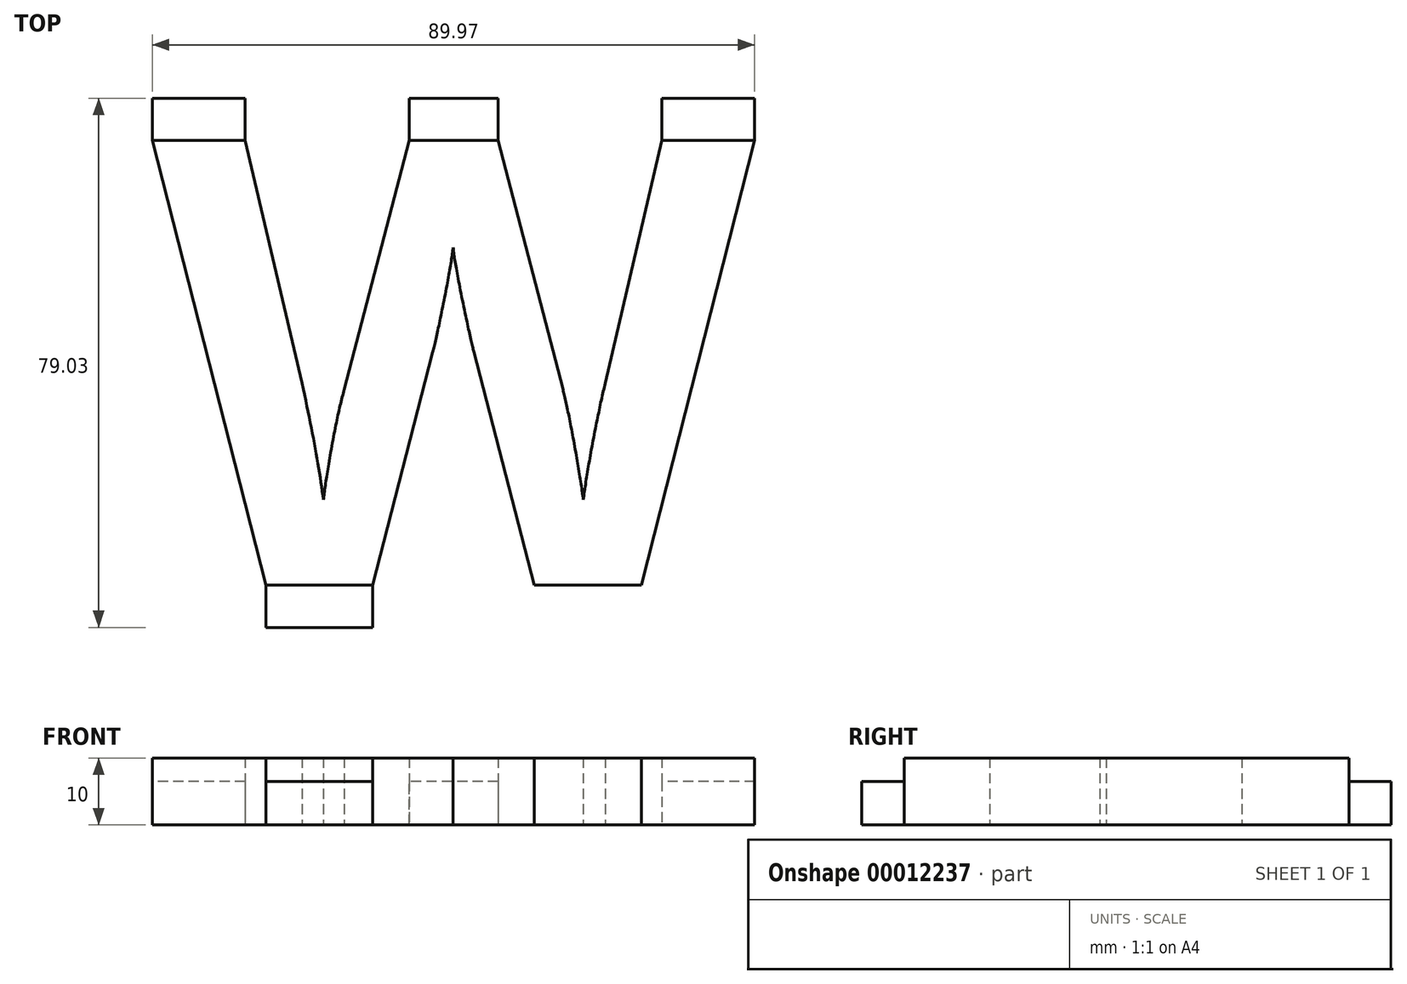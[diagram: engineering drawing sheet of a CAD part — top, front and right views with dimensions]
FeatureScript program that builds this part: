
annotation { "Feature Type Name" : "Feature", "Feature Type Description" : "" }
export const myFeature = defineFeature(function(context is Context, id is Id, definition is map)
    precondition{}
    {
        {
            var Q0;
            Q0=qCreatedBy(makeId("Top.planeOp"),FACE);
            var sketch = newSketch(context, id + "F0", { "sketchPlane" : qUnion([Q0])});
            skText(sketch, "E0", { "text": "W", "fontName": "OpenSans-Bold.ttf"});
            const initialGuessF0  = {"E0": [-0.08997, 0, 1, 0, 0.067]};
            skSetInitialGuess(sketch, initialGuessF0);
            skSolve(sketch);
        }
        {
            var Q0;
            Q0=makeQuery(id+"F0.imprint","IMPRINT",FACE,{"disambiguationData":[TD([[makeQuery(id+"F0.imprint","IMPRINT",EDGE,{"derivedFrom":sQuery(id+"F0.wireOp",EDGE,"E0.sketch_text.stroke-0")}),-1.0]])]});
            extrude(context, id + "F1", {"entities" : qUnion([Q0]), "depth" : 10 * mm});
        }
        {
            var Q0;
            Q0=makeQuery(id+"F1.opExtrude","SWEPT_FACE",FACE,{"disambiguationData":[OSD([sQuery(id+"F0.wireOp",EDGE,"E0.sketch_text.stroke-7")])]});
            var sketch = newSketch(context, id + "F2", { "sketchPlane" : qUnion([Q0])});
            skLineSegment(sketch, "E1.0.0", {"start": v(-73.02, 0) * mm, "end": v(-57.03, 0) * mm});
            skLineSegment(sketch, "E1.0.1", {"start": v(-57.03, 0) * mm, "end": v(-57.03, 10) * mm});
            skLineSegment(sketch, "E1.0.2", {"start": v(-57.03, 10) * mm, "end": v(-73.02, 10) * mm});
            skLineSegment(sketch, "E1.0.3", {"start": v(-73.02, 10) * mm, "end": v(-73.02, 0) * mm});
            skLineSegment(sketch, "E2.0.0", {"start": v(-32.95, 0) * mm, "end": v(-16.9, 0) * mm});
            skLineSegment(sketch, "E2.0.1", {"start": v(-16.9, 0) * mm, "end": v(-16.9, 10) * mm});
            skLineSegment(sketch, "E2.0.2", {"start": v(-16.9, 10) * mm, "end": v(-32.95, 10) * mm});
            skLineSegment(sketch, "E2.0.3", {"start": v(-32.95, 10) * mm, "end": v(-32.95, 0) * mm});
            skLineSegment(sketch, "E3.top", {"start": v(-73.02, 6.5) * mm, "end": v(-57.03, 6.5) * mm});
            skLineSegment(sketch, "E3.left", {"start": v(-73.02, 0) * mm, "end": v(-73.02, 6.5) * mm});
            skLineSegment(sketch, "E3.right", {"start": v(-57.03, 0) * mm, "end": v(-57.03, 6.5) * mm});
            skLineSegment(sketch, "E4.top", {"start": v(-32.95, 6.5) * mm, "end": v(-16.9, 6.5) * mm});
            skLineSegment(sketch, "E4.left", {"start": v(-32.95, 0) * mm, "end": v(-32.95, 6.5) * mm});
            skLineSegment(sketch, "E4.right", {"start": v(-16.9, 0) * mm, "end": v(-16.9, 6.5) * mm});
            skSolve(sketch);
        }
        {
            var Q0;
            Q0=makeQuery(id+"F2.imprint","IMPRINT",FACE,{"disambiguationData":[TD([[makeQuery(id+"F2.imprint","IMPRINT",EDGE,{"derivedFrom":sQuery(id+"F2.wireOp",EDGE,"E1.0.0")}),-1.0]])]});
            var Q1;
            Q1=makeQuery(id+"F2.imprint","IMPRINT",FACE,{"disambiguationData":[TD([[makeQuery(id+"F2.imprint","IMPRINT",EDGE,{"derivedFrom":sQuery(id+"F2.wireOp",EDGE,"E2.0.0")}),1.0]])]});
            extrude(context, id + "F3", {"entities" : qUnion([Q0, Q1]), "operationType" : NewBodyOperationType.ADD, "depth" : 6.3 * mm});
        }
        {
            var Q0;
            Q0=makeQuery(id+"F1.opExtrude","SWEPT_FACE",FACE,{"disambiguationData":[OSD([sQuery(id+"F0.wireOp",EDGE,"E0.sketch_text.stroke-22")])]});
            var sketch = newSketch(context, id + "F4", { "sketchPlane" : qUnion([Q0])});
            skLineSegment(sketch, "E5.0.0", {"start": v(0, 0) * mm, "end": v(13.87, 0) * mm});
            skLineSegment(sketch, "E5.0.1", {"start": v(13.87, 0) * mm, "end": v(13.87, 10) * mm});
            skLineSegment(sketch, "E5.0.2", {"start": v(13.87, 10) * mm, "end": v(0, 10) * mm});
            skLineSegment(sketch, "E5.0.3", {"start": v(0, 10) * mm, "end": v(0, 0) * mm});
            skLineSegment(sketch, "E6.0.0", {"start": v(38.31, 0) * mm, "end": v(51.62, 0) * mm});
            skLineSegment(sketch, "E6.0.1", {"start": v(51.62, 0) * mm, "end": v(51.62, 10) * mm});
            skLineSegment(sketch, "E6.0.2", {"start": v(51.62, 10) * mm, "end": v(38.31, 10) * mm});
            skLineSegment(sketch, "E6.0.3", {"start": v(38.31, 10) * mm, "end": v(38.31, 0) * mm});
            skLineSegment(sketch, "E7.0.0", {"start": v(76.12, 0) * mm, "end": v(89.97, 0) * mm});
            skLineSegment(sketch, "E7.0.1", {"start": v(89.97, 0) * mm, "end": v(89.97, 10) * mm});
            skLineSegment(sketch, "E7.0.2", {"start": v(89.97, 10) * mm, "end": v(76.12, 10) * mm});
            skLineSegment(sketch, "E7.0.3", {"start": v(76.12, 10) * mm, "end": v(76.12, 0) * mm});
            skLineSegment(sketch, "E8.top", {"start": v(0, 6.5) * mm, "end": v(13.87, 6.5) * mm});
            skLineSegment(sketch, "E8.left", {"start": v(0, 0) * mm, "end": v(0, 6.5) * mm});
            skLineSegment(sketch, "E8.right", {"start": v(13.87, 0) * mm, "end": v(13.87, 6.5) * mm});
            skLineSegment(sketch, "E9.top", {"start": v(38.31, 6.5) * mm, "end": v(51.62, 6.5) * mm});
            skLineSegment(sketch, "E9.left", {"start": v(38.31, 0) * mm, "end": v(38.31, 6.5) * mm});
            skLineSegment(sketch, "E9.right", {"start": v(51.62, 0) * mm, "end": v(51.62, 6.5) * mm});
            skLineSegment(sketch, "E10.top", {"start": v(76.12, 6.5) * mm, "end": v(89.97, 6.5) * mm});
            skLineSegment(sketch, "E10.left", {"start": v(76.12, 0) * mm, "end": v(76.12, 6.5) * mm});
            skLineSegment(sketch, "E10.right", {"start": v(89.97, 0) * mm, "end": v(89.97, 6.5) * mm});
            skSolve(sketch);
        }
        {
            var Q0;
            Q0=makeQuery(id+"F4.imprint","IMPRINT",FACE,{"disambiguationData":[TD([[makeQuery(id+"F4.imprint","IMPRINT",EDGE,{"derivedFrom":sQuery(id+"F4.wireOp",EDGE,"E5.0.0")}),-1.0]])]});
            var Q1;
            Q1=makeQuery(id+"F4.imprint","IMPRINT",FACE,{"disambiguationData":[TD([[makeQuery(id+"F4.imprint","IMPRINT",EDGE,{"derivedFrom":sQuery(id+"F4.wireOp",EDGE,"E6.0.0")}),1.0]])]});
            var Q2;
            Q2=makeQuery(id+"F4.imprint","IMPRINT",FACE,{"disambiguationData":[TD([[makeQuery(id+"F4.imprint","IMPRINT",EDGE,{"derivedFrom":sQuery(id+"F4.wireOp",EDGE,"E7.0.0")}),1.0]])]});
            extrude(context, id + "F5", {"entities" : qUnion([Q0, Q1, Q2]), "operationType" : NewBodyOperationType.ADD, "depth" : 6.3 * mm});
        }
    });
